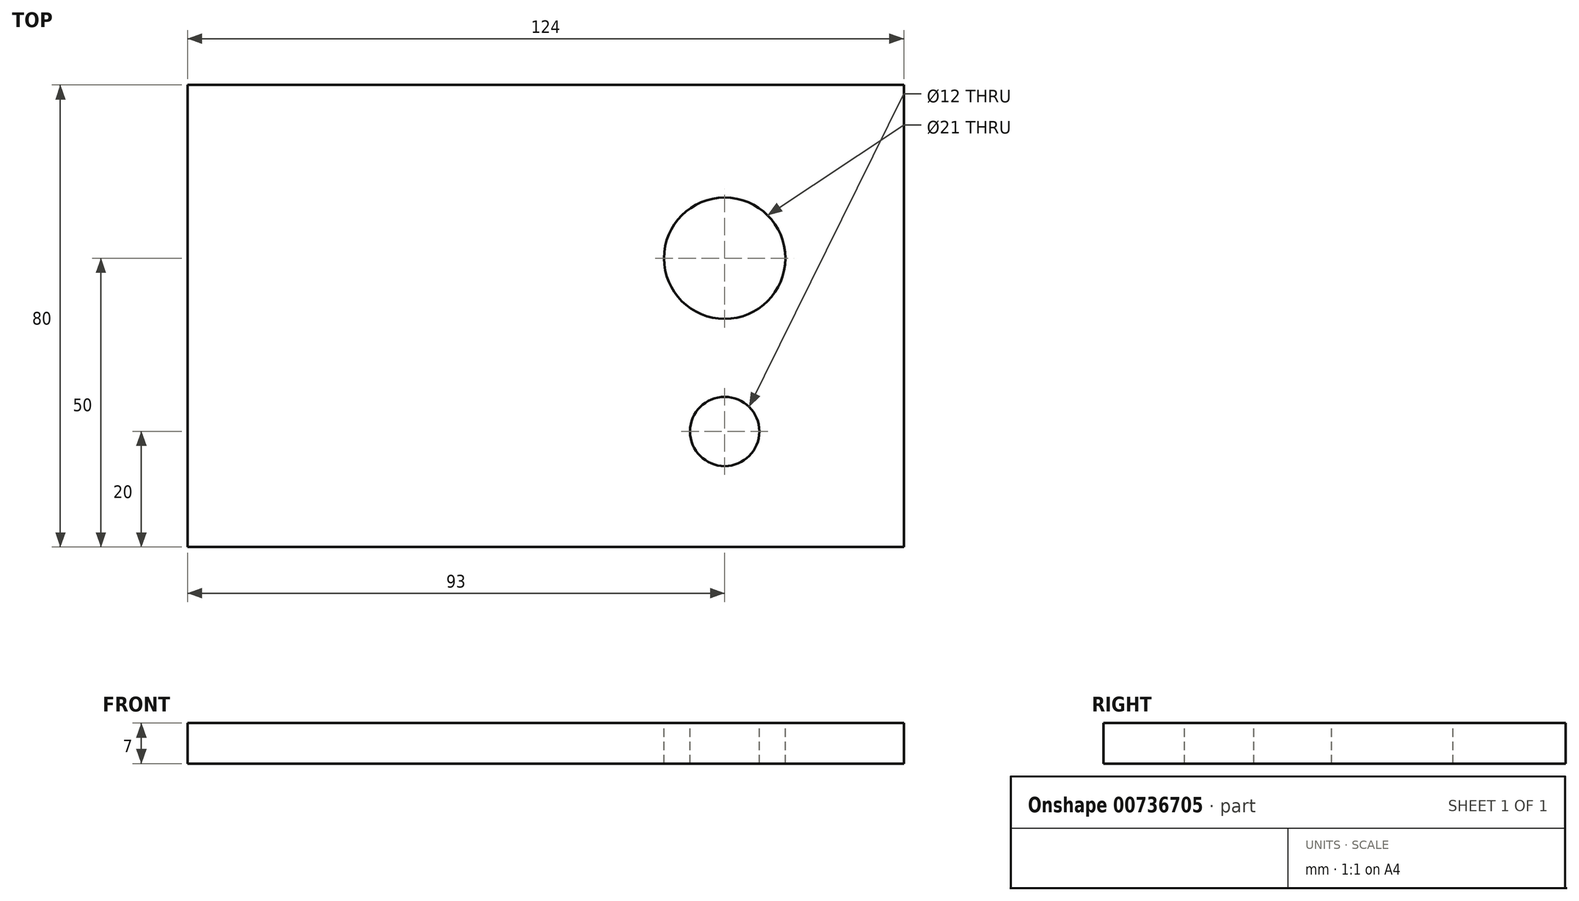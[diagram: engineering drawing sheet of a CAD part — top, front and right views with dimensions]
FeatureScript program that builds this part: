
annotation { "Feature Type Name" : "Feature", "Feature Type Description" : "" }
export const myFeature = defineFeature(function(context is Context, id is Id, definition is map)
    precondition{}
    {
        {
            var Q0;
            Q0=qCreatedBy(makeId("Top.planeOp"),FACE);
            var sketch = newSketch(context, id + "F0", { "sketchPlane" : qUnion([Q0])});
            skLineSegment(sketch, "E0.bottom", {"start": v(0, 0) * mm, "end": v(-124, 0) * mm});
            skLineSegment(sketch, "E0.top", {"start": v(0, 80) * mm, "end": v(-124, 80) * mm});
            skLineSegment(sketch, "E0.left", {"start": v(0, 0) * mm, "end": v(0, 80) * mm});
            skLineSegment(sketch, "E0.right", {"start": v(-124, 0) * mm, "end": v(-124, 80) * mm});
            skSolve(sketch);
        }
        {
            var Q0;
            Q0 = qSketchRegion(id + "F0", true);
            var Q1;
            Q1=makeQuery(id+"F0.imprint","IMPRINT",FACE,{"disambiguationData":[TD([[makeQuery(id+"F0.imprint","IMPRINT",EDGE,{"derivedFrom":sQuery(id+"F0.wireOp",EDGE,"E0.bottom")}),-1.0]])]});
            extrude(context, id + "F1", {"entities" : qUnion([Q0, Q1]), "oppositeDirection" : true, "depth" : 7 * mm, "offsetDistance" : 25 * mm});
        }
        {
            var Q0;
            Q0=makeQuery(id+"F1.opExtrude","SWEPT_BODY",BODY,{"disambiguationData":[OSD([sQuery(id+"F0.wireOp",EDGE,"E0.bottom"),sQuery(id+"F0.wireOp",EDGE,"E0.top"),sQuery(id+"F0.wireOp",EDGE,"E0.left"),sQuery(id+"F0.wireOp",EDGE,"E0.right")])]});
            transform(context, id + "F2", {"entities" : qUnion([Q0]), "transformType" : TransformType.TRANSLATION_3D, "dx" : 0 * mm, "dy" : 0 * mm, "dz" : 0 * mm, "makeCopy" : true});
        }
        {
            var Q0;
            Q0=makeQuery(id+"F1.opExtrude","SWEPT_BODY",BODY,{"disambiguationData":[OSD([sQuery(id+"F0.wireOp",EDGE,"E0.bottom"),sQuery(id+"F0.wireOp",EDGE,"E0.top"),sQuery(id+"F0.wireOp",EDGE,"E0.left"),sQuery(id+"F0.wireOp",EDGE,"E0.right")])]});
            deleteBodies(context, id + "F3", {"entities" : qUnion([Q0])});
        }
        {
            var Q0;
            Q0=makeQuery(id+"F2.opPattern","COPY",FACE,{"derivedFrom":makeQuery(id+"F1.opExtrude","CAP_FACE",FACE,{"disambiguationData":[OSD([sQuery(id+"F0.wireOp",EDGE,"E0.bottom"),sQuery(id+"F0.wireOp",EDGE,"E0.top"),sQuery(id+"F0.wireOp",EDGE,"E0.left"),sQuery(id+"F0.wireOp",EDGE,"E0.right")])],"isStart":true}),"instanceName":"1"});
            var sketch = newSketch(context, id + "F4", { "sketchPlane" : qUnion([Q0])});
            skLineSegment(sketch, "E1", {"start": v(-62, 0) * mm, "end": v(-62, 80) * mm});
            skLineSegment(sketch, "E2", {"start": v(-31, 40) * mm, "end": v(-31, 20) * mm});
            skLineSegment(sketch, "E3", {"start": v(-31, 40) * mm, "end": v(-31, 50) * mm});
            skCircle(sketch, "E4", {"center": v(-31, 20) * mm, "radius": 6 * mm});
            skCircle(sketch, "E5", {"center": v(-31, 50) * mm, "radius": 10.5 * mm});
            skSolve(sketch);
        }
        {
            var Q0;
            Q0=makeQuery(id+"F4.imprint","IMPRINT",FACE,{"disambiguationData":[TD([[makeQuery(id+"F4.imprint","IMPRINT",EDGE,{"derivedFrom":sQuery(id+"F4.wireOp",EDGE,"E5")}),1.0]])]});
            var Q1;
            Q1=makeQuery(id+"F4.imprint","IMPRINT",FACE,{"disambiguationData":[TD([[makeQuery(id+"F4.imprint","IMPRINT",EDGE,{"derivedFrom":sQuery(id+"F4.wireOp",EDGE,"E4")}),1.0]])]});
            extrude(context, id + "F5", {"entities" : qUnion([Q0, Q1]), "operationType" : NewBodyOperationType.REMOVE, "oppositeDirection" : true, "depth" : 25 * mm, "offsetDistance" : 25 * mm});
        }
    });
